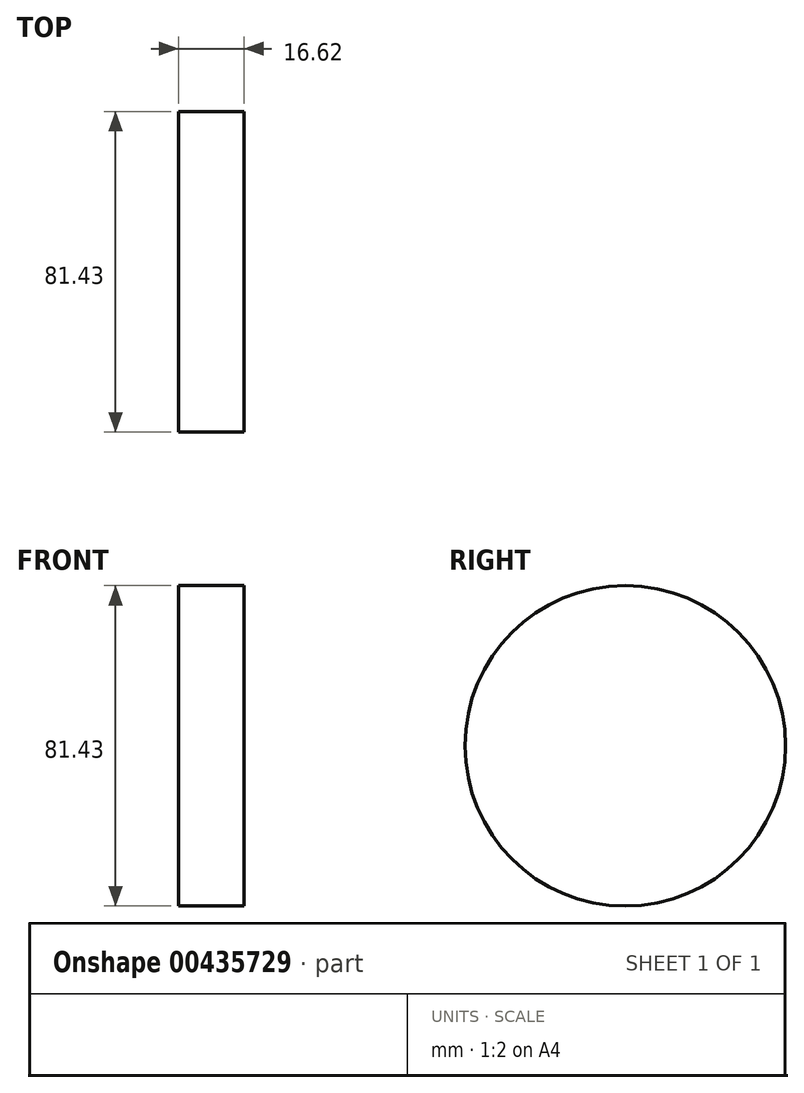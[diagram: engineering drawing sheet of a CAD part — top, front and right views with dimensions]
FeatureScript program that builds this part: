
annotation { "Feature Type Name" : "Feature", "Feature Type Description" : "" }
export const myFeature = defineFeature(function(context is Context, id is Id, definition is map)
    precondition{}
    {
        {
            var Q0;
            Q0=qCreatedBy(makeId("Right.planeOp"),FACE);
            var sketch = newSketch(context, id + "F0", { "sketchPlane" : qUnion([Q0])});
            skCircle(sketch, "E0", {"center": v(0.47, -0.21) * mm, "radius": 40.71 * mm});
            skPoint(sketch, "E0.first.point", {"position": v(-27.95, 28.94) * mm});
            skPoint(sketch, "E0.second.point", {"position": v(29.57, -28.7) * mm});
            skPoint(sketch, "E0.third.point", {"position": v(41.19, 0) * mm});
            skSolve(sketch);
        }
        {
            var Q0;
            Q0=makeQuery(id+"F0.imprint","IMPRINT",FACE,{"disambiguationData":[TD([[makeQuery(id+"F0.imprint","IMPRINT",EDGE,{"derivedFrom":sQuery(id+"F0.wireOp",EDGE,"E0")}),1.0]])]});
            extrude(context, id + "F1", {"entities" : qUnion([Q0]), "depth" : 16.62 * mm});
        }
    });
